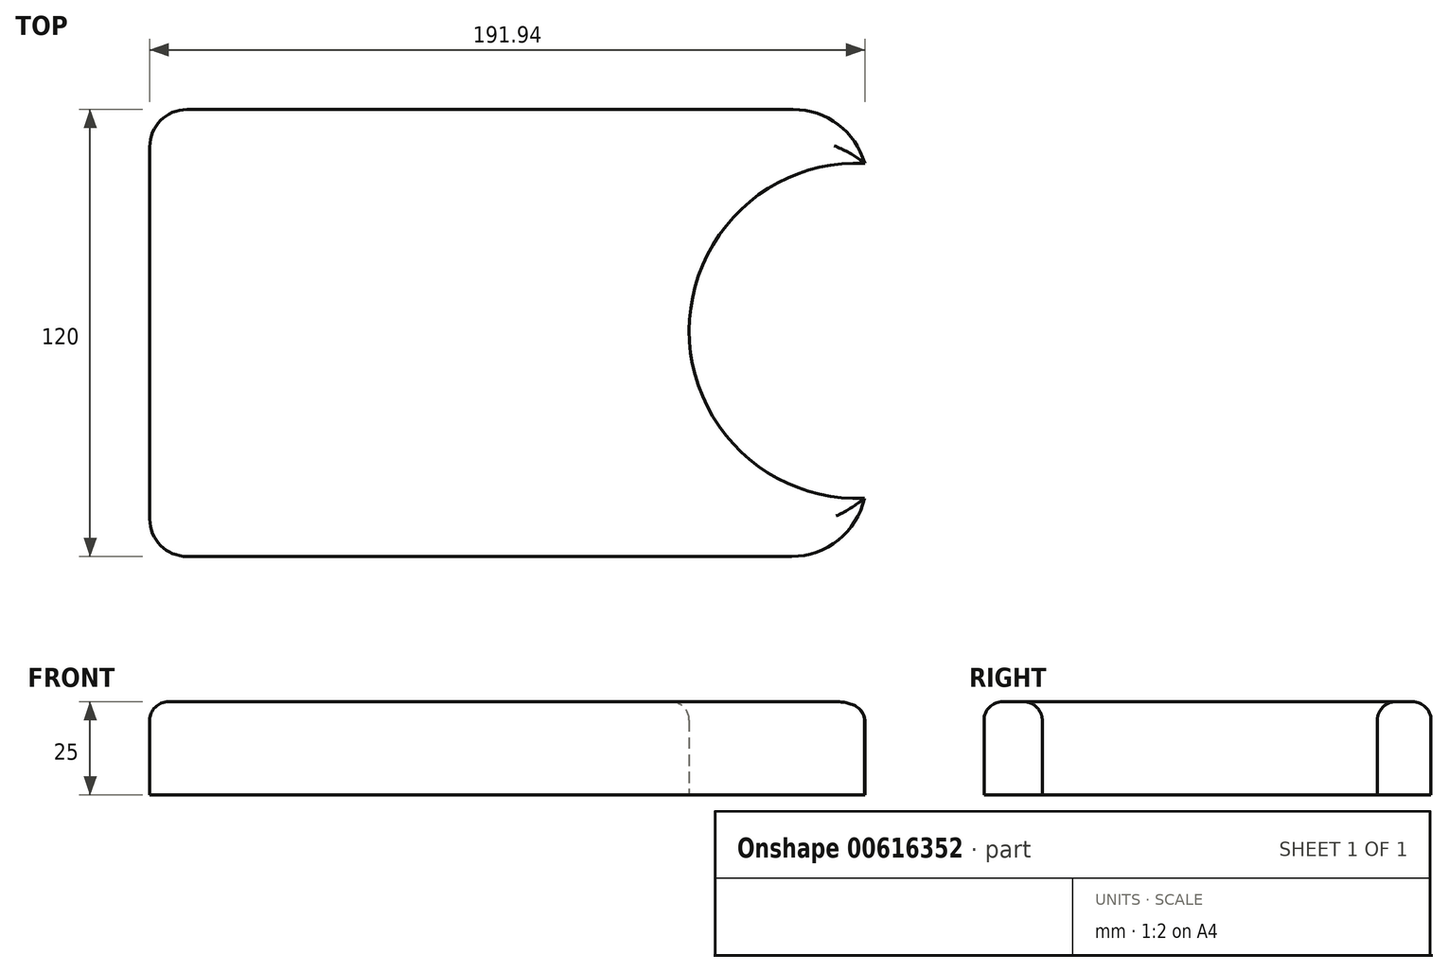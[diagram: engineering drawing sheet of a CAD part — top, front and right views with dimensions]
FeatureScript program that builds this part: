
annotation { "Feature Type Name" : "Feature", "Feature Type Description" : "" }
export const myFeature = defineFeature(function(context is Context, id is Id, definition is map)
    precondition{}
    {
        {
            var Q0;
            Q0=qCreatedBy(makeId("Top.planeOp"),FACE);
            var sketch = newSketch(context, id + "F0", { "sketchPlane" : qUnion([Q0])});
            skLineSegment(sketch, "E0.bottom", {"start": v(-89.45, 59.83) * mm, "end": v(73.27, 59.83) * mm});
            skLineSegment(sketch, "E0.top", {"start": v(-89.45, -60.17) * mm, "end": v(72.86, -60.17) * mm});
            skLineSegment(sketch, "E0.left", {"start": v(-99.45, 49.83) * mm, "end": v(-99.45, -50.17) * mm});
            skArc(sketch, "E1.filletArc", {"start": v(92.49, 45.38) * mm, "mid": v(85.3, 55.81) * mm, "end": v(73.27, 59.83) * mm});
            skArc(sketch, "E2.filletArc", {"start": v(72.86, -60.17) * mm, "mid": v(85.37, -55.78) * mm, "end": v(92.38, -44.53) * mm});
            skPoint(sketch, "E3.visualSharp", {"position": v(-99.45, 59.83) * mm});
            skArc(sketch, "E3.filletArc", {"start": v(-89.45, 59.83) * mm, "mid": v(-96.52, 56.9) * mm, "end": v(-99.45, 49.83) * mm});
            skPoint(sketch, "E4.visualSharp", {"position": v(-99.45, -60.17) * mm});
            skArc(sketch, "E4.filletArc", {"start": v(-99.45, -50.17) * mm, "mid": v(-96.52, -57.24) * mm, "end": v(-89.45, -60.17) * mm});
            skArc(sketch, "E5", {"start": v(92.49, 45.38) * mm, "mid": v(45.35, 0.48) * mm, "end": v(92.38, -44.53) * mm});
            skLineSegment(sketch, "E6", {"start": v(-99.45, -0.17) * mm, "end": v(90.35, 0.43) * mm, "construction": true});
            skSolve(sketch);
        }
        {
            var Q0;
            Q0 = qSketchRegion(id + "F0", true);
            extrude(context, id + "F1", {"entities" : qUnion([Q0]), "depth" : 25 * mm, "offsetDistance" : 25 * mm});
        }
        {
            var Q0;
            Q0=makeQuery(id+"F1.opExtrude","CAP_EDGE",EDGE,{"disambiguationData":[OSD([sQuery(id+"F0.wireOp",EDGE,"E0.bottom")])],"isStart":false});
            var Q1;
            Q1=makeQuery(id+"F1.opExtrude","CAP_EDGE",EDGE,{"disambiguationData":[OSD([sQuery(id+"F0.wireOp",EDGE,"E0.left")])],"isStart":false});
            var Q2;
            Q2=makeQuery(id+"F1.opExtrude","CAP_EDGE",EDGE,{"disambiguationData":[OSD([sQuery(id+"F0.wireOp",EDGE,"E0.top")])],"isStart":false});
            var Q3;
            Q3=makeQuery(id+"F1.opExtrude","CAP_EDGE",EDGE,{"disambiguationData":[OSD([sQuery(id+"F0.wireOp",EDGE,"E5")])],"isStart":false});
            fillet(context, id + "F2", {"entities" : qUnion([Q0, Q1, Q2, Q3]), "radius" : 5 * mm, "tangentPropagation" : true, "allowEdgeOverflow" : false});
        }
    });
